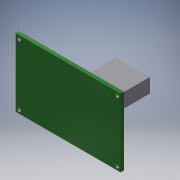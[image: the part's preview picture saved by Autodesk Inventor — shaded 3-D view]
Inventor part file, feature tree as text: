
AUTODESK INVENTOR PART (.ipt)
format: ipt  version: 2018 (Build 220112000, 112)  size: 148,480 bytes
history: native  units: mm
features: extrude x4, sketch x4
ambient origin geometry x8: Origin, YZ Plane, XZ Plane, XY Plane, X Axis, Y Axis, Z Axis, Center Point
bodies: Solid1 (feature_tree)
feature tree (8):
  extrude  "Extrusion1"  Depth=59.0mm
  extrude  "Extrusion2"  Depth=2.5mm
  extrude  "Extrusion3"  Depth=48.0mm
  extrude  "Extrusion4"  Depth=10.0mm TaperAngle=0.0deg
  sketch  "Sketch1"  dims[d0=91.0mm d1=59.0mm]
  sketch  "Sketch2"  dims[d2=3.0mm d3=0.0mm d4=2.5mm]
  sketch  "Sketch3"  dims[d5=7.0mm d6=48.0mm]
  sketch  "Sketch4"  dims[d7=20.4mm d8=10.0mm d9=0.0mm d10=1.7mm d11=22.1mm d12=15.3mm d13=3.3mm d14=12.4mm d15=29.3mm d16=12.5mm d17=12.7mm d18=85.0mm d19=53.0mm d20=3.2mm d21=3.2mm d22=3.2mm d23=3.2mm d24=3.0mm d25=0.0mm d26=25.0mm d27=0.0mm]
